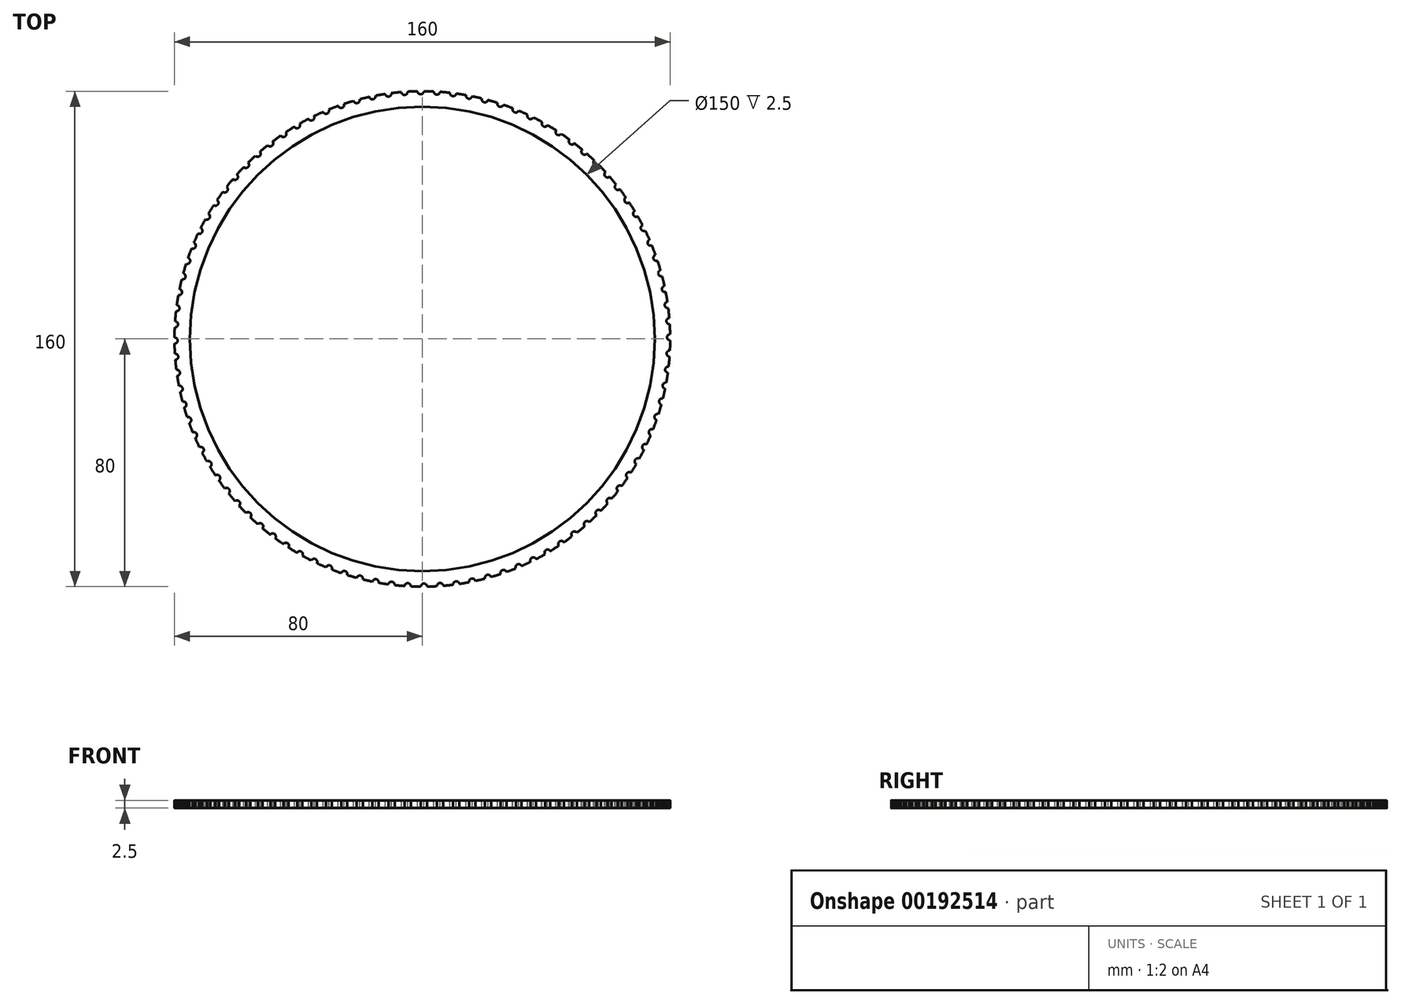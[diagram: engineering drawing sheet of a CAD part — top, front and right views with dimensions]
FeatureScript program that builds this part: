
annotation { "Feature Type Name" : "Feature", "Feature Type Description" : "" }
export const myFeature = defineFeature(function(context is Context, id is Id, definition is map)
    precondition{}
    {
        {
            var Q0;
            Q0=qCreatedBy(makeId("Top.planeOp"),FACE);
            var sketch = newSketch(context, id + "F0", { "sketchPlane" : qUnion([Q0])});
            skCircle(sketch, "E0", {"center": v(0, 0) * mm, "radius": 80 * mm});
            skCircle(sketch, "E1", {"center": v(0, 0) * mm, "radius": 75 * mm});
            skSolve(sketch);
        }
        {
            var Q0;
            Q0 = qSketchRegion(id + "F0", true);
            extrude(context, id + "F1", {"entities" : qUnion([Q0]), "depth" : 2.5 * mm});
        }
        {
            var Q0;
            Q0=makeQuery(id+"F1.opExtrude","CAP_FACE",FACE,{"disambiguationData":[OSD([sQuery(id+"F0.wireOp",EDGE,"E0"),sQuery(id+"F0.wireOp",EDGE,"E1")])],"isStart":false});
            var sketch = newSketch(context, id + "F2", { "sketchPlane" : qUnion([Q0])});
            skCircle(sketch, "E2", {"center": v(-71.52, -35.85) * mm, "radius": 1 * mm});
            skSolve(sketch);
        }
        {
            var Q0;
            {var subQ0=sQuery(id+"F2.wireOp",EDGE,"E2");var subQ1=makeQuery(id+"F1.opExtrude","CAP_EDGE",EDGE,{"disambiguationData":[OSD([sQuery(id+"F0.wireOp",EDGE,"E0")])],"isStart":false});var subQ2=makeQuery(id+"F2.imprint","INTERSECT",VERTEX,{"disambiguationData":[OD(0.0)],"derivedFrom":[subQ1,subQ0]});Q0=makeQuery(id+"F2.imprint","IMPRINT",FACE,{"disambiguationData":[TD([[makeQuery(id+"F2.imprint","IMPRINT",EDGE,{"disambiguationData":[TD([[subQ2,1.0]])],"derivedFrom":subQ0}),1.0]])]});}
            extrude(context, id + "F3", {"entities" : qUnion([Q0]), "operationType" : NewBodyOperationType.REMOVE, "endBound" : BoundingType.THROUGH_ALL, "oppositeDirection" : true, "depth" : 25 * mm});
        }
        {
            var Q0;
            Q0=makeQuery(id+"F3.boolean.opBoolean","COPY",FACE,{"derivedFrom":makeQuery(id+"F3.opExtrude","SWEPT_FACE",FACE,{"disambiguationData":[OSD([sQuery(id+"F2.wireOp",EDGE,"E2")])]})});
            var Q1;
            Q1=makeQuery(id+"F1.opExtrude","SWEPT_FACE",FACE,{"disambiguationData":[OSD([sQuery(id+"F0.wireOp",EDGE,"E0")])]});
            circularPattern(context, id + "F4", {"patternType" : PatternType.FACE, "faces" : qUnion([Q0]), "axis" : qUnion([Q1]), "angle" : 360 * degree, "instanceCount" : 96, "equalSpace" : true});
        }
        {
            var Q0;
            Q0=makeQuery(id+"F1.opExtrude","CAP_FACE",FACE,{"disambiguationData":[OSD([sQuery(id+"F0.wireOp",EDGE,"E0"),sQuery(id+"F0.wireOp",EDGE,"E1")])],"isStart":false});
            var sketch = newSketch(context, id + "F5", { "sketchPlane" : qUnion([Q0])});
            skLineSegment(sketch, "E3.bottom", {"start": v(-75, -0.78) * mm, "end": v(-83, -0.78) * mm});
            skLineSegment(sketch, "E3.top", {"start": v(-75, -0.28) * mm, "end": v(-83, -0.28) * mm});
            skLineSegment(sketch, "E3.left", {"start": v(-75, -0.78) * mm, "end": v(-75, -0.28) * mm});
            skLineSegment(sketch, "E3.right", {"start": v(-83, -0.78) * mm, "end": v(-83, -0.28) * mm});
            skPoint(sketch, "E3.middle", {"position": v(-79, -0.53) * mm});
            skPoint(sketch, "E3.middle.positionSnap0", {"position": v(-79, -0.51) * mm});
            skPoint(sketch, "E3.centerSnap0", {"position": v(-79, -0.51) * mm});
            skSolve(sketch);
        }
        {
            var Q0;
            {var subQ3=makeQuery(id+"F4.opPattern","COPY",EDGE,{"derivedFrom":makeQuery(id+"F3.boolean.opBoolean","COPY",EDGE,{"derivedFrom":makeQuery(id+"F3.opExtrude","CAP_EDGE",EDGE,{"disambiguationData":[OSD([sQuery(id+"F2.wireOp",EDGE,"E2")])],"isStart":true})}),"instanceName":"7"});var subQ5=sQuery(id+"F5.wireOp",EDGE,"E3.top");var subQ6=makeQuery(id+"F5.imprint","INTERSECT",VERTEX,{"derivedFrom":[subQ3,subQ5]});Q0=makeQuery(id+"F5.imprint","IMPRINT",FACE,{"disambiguationData":[TD([[makeQuery(id+"F5.imprint","IMPRINT",EDGE,{"disambiguationData":[TD([[subQ6,1.0]])],"derivedFrom":subQ5}),1.0]])]});}
            extrude(context, id + "F6", {"entities" : qUnion([Q0]), "operationType" : NewBodyOperationType.REMOVE, "oppositeDirection" : true, "depth" : 0.5 * mm});
        }
    });
